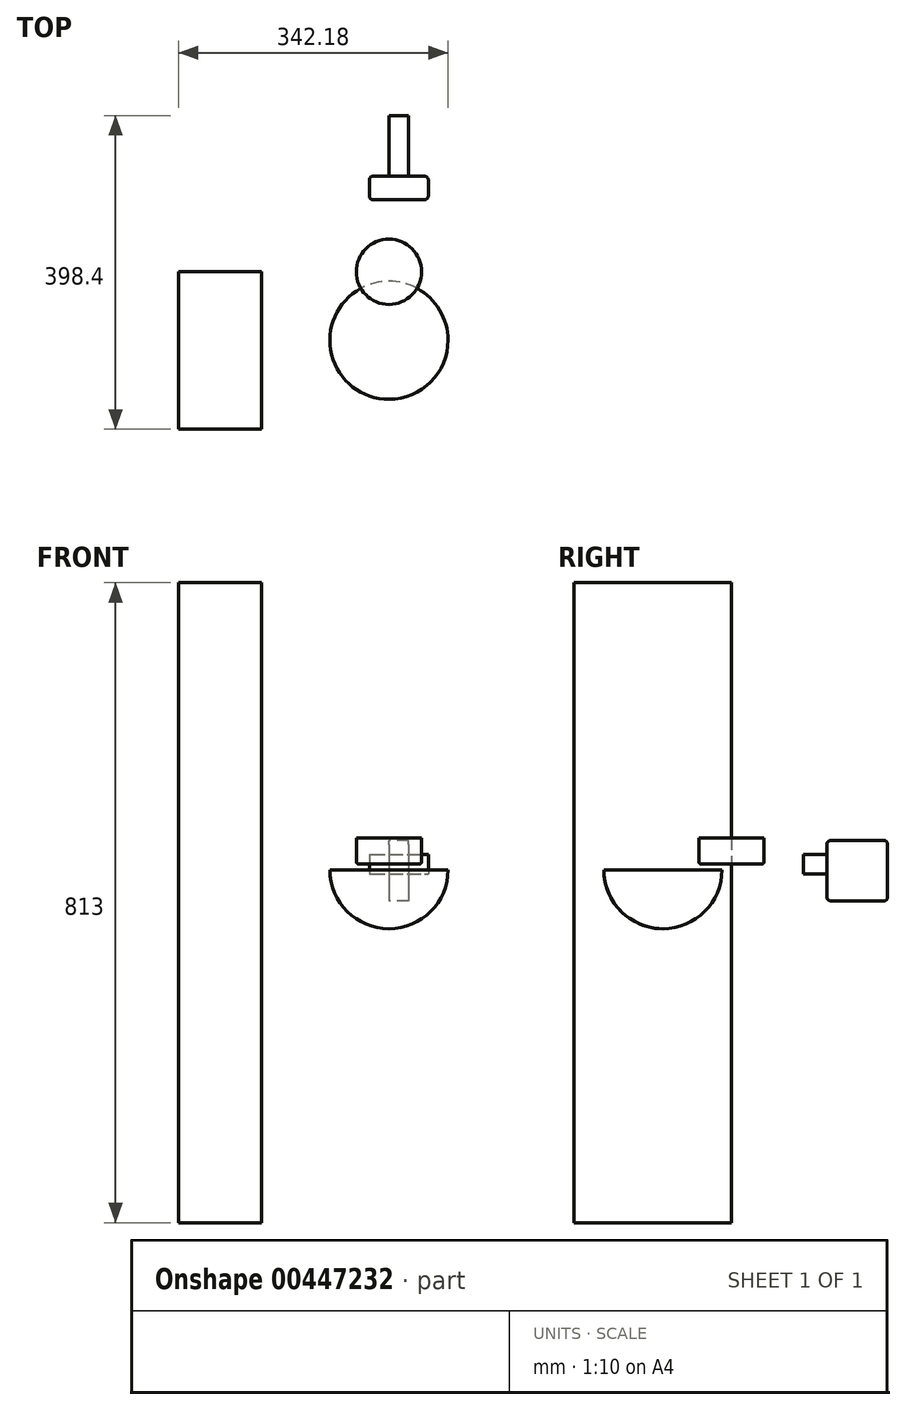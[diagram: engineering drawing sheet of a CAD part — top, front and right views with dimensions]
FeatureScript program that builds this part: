
annotation { "Feature Type Name" : "Feature", "Feature Type Description" : "" }
export const myFeature = defineFeature(function(context is Context, id is Id, definition is map)
    precondition{}
    {
        {
            var Q0;
            Q0=qCreatedBy(makeId("Top.planeOp"),FACE);
            var sketch = newSketch(context, id + "F0", { "sketchPlane" : qUnion([Q0])});
            skCircle(sketch, "E0", {"center": v(0, 0) * mm, "radius": 41.5 * mm});
            skSolve(sketch);
        }
        {
            var Q0;
            Q0=makeQuery(id+"F0.imprint","IMPRINT",FACE,{"disambiguationData":[TD([[makeQuery(id+"F0.imprint","IMPRINT",EDGE,{"derivedFrom":sQuery(id+"F0.wireOp",EDGE,"E0")}),1.0]])]});
            extrude(context, id + "F1", {"entities" : qUnion([Q0]), "depth" : 33 * mm});
        }
        {
            var Q0;
            Q0=makeQuery(id+"F1.opExtrude","CAP_EDGE",EDGE,{"disambiguationData":[OSD([sQuery(id+"F0.wireOp",EDGE,"E0")])],"isStart":true});
            fillet(context, id + "F2", {"entities" : qUnion([Q0]), "radius" : 3 * mm, "tangentPropagation" : true, "allowEdgeOverflow" : false});
        }
        {
            var Q0;
            Q0=qCreatedBy(makeId("Right.planeOp"),FACE);
            var sketch = newSketch(context, id + "F3", { "sketchPlane" : qUnion([Q0])});
            skLineSegment(sketch, "E1", {"start": v(-162.03, -7.22) * mm, "end": v(-12.03, -7.22) * mm});
            skArc(sketch, "E2", {"start": v(-162.03, -7.22) * mm, "mid": v(-87.03, -82.22) * mm, "end": v(-12.03, -7.22) * mm});
            skLineSegment(sketch, "E3", {"start": v(-87.03, -7.22) * mm, "end": v(-87.03, -89.52) * mm});
            skSolve(sketch);
        }
        {
            var Q0;
            {var subQ0=sQuery(id+"F3.wireOp",EDGE,"E2");var subQ1=sQuery(id+"F3.wireOp",EDGE,"E1");var subQ2=makeQuery(id+"F3.imprint","INTERSECT",VERTEX,{"disambiguationData":[OD(0.0)],"derivedFrom":[subQ1,subQ0]});Q0=makeQuery(id+"F3.imprint","IMPRINT",FACE,{"disambiguationData":[TD([[makeQuery(id+"F3.imprint","IMPRINT",EDGE,{"disambiguationData":[TD([[subQ2,-1.0]])],"derivedFrom":subQ1}),-1.0]])]});}
            var Q1;
            Q1=sQuery(id+"F3.wireOp",EDGE,"E3");
            revolve(context, id + "F4", {"entities" : qUnion([Q0]), "axis" : qUnion([Q1]), "revolveType" : RevolveType.FULL});
        }
        {
            var Q0;
            Q0=qCreatedBy(makeId("Right.planeOp"),FACE);
            var sketch = newSketch(context, id + "F5", { "sketchPlane" : qUnion([Q0])});
            skLineSegment(sketch, "E4.bottom", {"start": v(126.4, 30.05) * mm, "end": v(193.4, 30.05) * mm});
            skLineSegment(sketch, "E4.top", {"start": v(126.4, -46.95) * mm, "end": v(193.4, -46.95) * mm});
            skLineSegment(sketch, "E4.left", {"start": v(121.4, 25.05) * mm, "end": v(121.4, -41.95) * mm});
            skLineSegment(sketch, "E4.right", {"start": v(198.4, 25.05) * mm, "end": v(198.4, -41.95) * mm});
            skPoint(sketch, "E5.visualSharp", {"position": v(121.4, 30.05) * mm});
            skArc(sketch, "E5.filletArc", {"start": v(126.4, 30.05) * mm, "mid": v(122.86, 28.59) * mm, "end": v(121.4, 25.05) * mm});
            skPoint(sketch, "E6.visualSharp", {"position": v(198.4, 30.05) * mm});
            skArc(sketch, "E6.filletArc", {"start": v(198.4, 25.05) * mm, "mid": v(196.93, 28.59) * mm, "end": v(193.4, 30.05) * mm});
            skPoint(sketch, "E7.visualSharp", {"position": v(198.4, -46.95) * mm});
            skArc(sketch, "E7.filletArc", {"start": v(193.4, -46.95) * mm, "mid": v(196.93, -45.48) * mm, "end": v(198.4, -41.95) * mm});
            skPoint(sketch, "E8.visualSharp", {"position": v(121.4, -46.95) * mm});
            skArc(sketch, "E8.filletArc", {"start": v(121.4, -41.95) * mm, "mid": v(122.86, -45.48) * mm, "end": v(126.4, -46.95) * mm});
            skSolve(sketch);
        }
        {
            var Q0;
            Q0=makeQuery(id+"F5.imprint","IMPRINT",FACE,{"disambiguationData":[TD([[makeQuery(id+"F5.imprint","IMPRINT",EDGE,{"derivedFrom":sQuery(id+"F5.wireOp",EDGE,"E4.bottom")}),-1.0]])]});
            extrude(context, id + "F6", {"entities" : qUnion([Q0]), "depth" : 25 * mm});
        }
        {
            var Q0;
            Q0=qCreatedBy(makeId("Top.planeOp"),FACE);
            var sketch = newSketch(context, id + "F7", { "sketchPlane" : qUnion([Q0])});
            skLineSegment(sketch, "E9.bottom", {"start": v(-20, 121.4) * mm, "end": v(45, 121.4) * mm});
            skLineSegment(sketch, "E9.top", {"start": v(-20, 91.4) * mm, "end": v(45, 91.4) * mm});
            skLineSegment(sketch, "E9.left", {"start": v(-25, 116.4) * mm, "end": v(-25, 96.4) * mm});
            skLineSegment(sketch, "E9.right", {"start": v(50, 116.4) * mm, "end": v(50, 96.4) * mm});
            skPoint(sketch, "E10.visualSharp", {"position": v(-25, 121.4) * mm});
            skArc(sketch, "E10.filletArc", {"start": v(-20, 121.4) * mm, "mid": v(-23.54, 119.93) * mm, "end": v(-25, 116.4) * mm});
            skPoint(sketch, "E11.visualSharp", {"position": v(-25, 91.4) * mm});
            skArc(sketch, "E11.filletArc", {"start": v(-25, 96.4) * mm, "mid": v(-23.54, 92.86) * mm, "end": v(-20, 91.4) * mm});
            skPoint(sketch, "E12.visualSharp", {"position": v(50, 91.4) * mm});
            skArc(sketch, "E12.filletArc", {"start": v(45, 91.4) * mm, "mid": v(48.54, 92.86) * mm, "end": v(50, 96.4) * mm});
            skPoint(sketch, "E13.visualSharp", {"position": v(50, 121.4) * mm});
            skArc(sketch, "E13.filletArc", {"start": v(50, 116.4) * mm, "mid": v(48.54, 119.93) * mm, "end": v(45, 121.4) * mm});
            skSolve(sketch);
        }
        {
            var Q0;
            Q0=makeQuery(id+"F7.imprint","IMPRINT",FACE,{"disambiguationData":[TD([[makeQuery(id+"F7.imprint","IMPRINT",EDGE,{"derivedFrom":sQuery(id+"F7.wireOp",EDGE,"E9.bottom")}),-1.0]])]});
            extrude(context, id + "F8", {"entities" : qUnion([Q0]), "operationType" : NewBodyOperationType.ADD, "depth" : 25 * mm, "symmetric" : true});
        }
        {
            var Q0;
            Q0=qCreatedBy(makeId("Front.planeOp"),FACE);
            var sketch = newSketch(context, id + "F9", { "sketchPlane" : qUnion([Q0])});
            skLineSegment(sketch, "E14.bottom", {"start": v(-267.18, 357.44) * mm, "end": v(-161.75, 357.44) * mm});
            skLineSegment(sketch, "E14.top", {"start": v(-267.18, -455.56) * mm, "end": v(-161.75, -455.56) * mm});
            skLineSegment(sketch, "E14.left", {"start": v(-267.18, 357.44) * mm, "end": v(-267.18, -455.56) * mm});
            skLineSegment(sketch, "E14.right", {"start": v(-161.75, 357.44) * mm, "end": v(-161.75, -455.56) * mm});
            skSolve(sketch);
        }
        {
            var Q0;
            Q0=makeQuery(id+"F9.imprint","IMPRINT",FACE,{"disambiguationData":[TD([[makeQuery(id+"F9.imprint","IMPRINT",EDGE,{"derivedFrom":sQuery(id+"F9.wireOp",EDGE,"E14.bottom")}),-1.0]])]});
            extrude(context, id + "F10", {"entities" : qUnion([Q0]), "depth" : 200 * mm});
        }
    });
